# Revit family: Plumbing-Flushometer-Sloan-Valve-Royal-611-ESS-WB_
name_source: partatom
category: Plumbing Fixtures
units: mm (PartAtom-declared; Revit-internal decimal feet)

## family parameters
Cut with Voids When Loaded = Yes
Host = Face
Maintain Annotation Orientation = No
OmniClass Number = 23.45.05.14.99
Part Type = Normal
Room Calculation Point = No
Round Connector Dimension = Use Diameter
Shared = No

## types (3) — shared parameters
Apparent Load = 0 VA
Assembly Code = D2020300
CW Connection = Yes
Centerline of Supply from Top of Fixture = 14 1/2"
Centerline of Supply to Centerline of Valve = 5"
Connector Description = Electrical Connection
Current = 0 A
Default Elevation = 0"
Edition number = 1
HW Connection = No
Hardwired = Yes
Keynote = 15410
L Dimension = 3"
Manufacturer = Sloan Valve
Number of Poles = 1
Operating Water Pressure = 15 – 80 PSI (103 – 552 kPa)
Power Factor = 1
Product data url = https://bimobject.com
URL = www.sloanvalve.com
Valve Pressure Drop = 0.00 psi
Vent Connection = No
Version = 1
Voltage = 24 V
Waste Connection = No
Water Inlet Connection Description = Water Inlet Connection
Water Inlet Connection Diameter = 1"
zero-valued in all types: CWFU, HWFU, WFU

## per-type parameters (varying)
| type | Description | Flush Rate | Part Number | Product Material |
| ROYAL 611 ESS WB-1.28-HW | 1.28 gpf, Rough Brass Finish, Fixture Connection Rear Spud, Single Flush, Electrical Override, Hardwired, Sensor-Operated, Front Accessible Wall Box, Royal® Concealed Sensor Hardwired Water Closet Flushometer. | 1.28 gpf (4.8 Lpf) | 34581001 | Sloan Valve - Finish - Polished Chrome |
| ROYAL 611 ESS WB-1.6-HW | 1.6 gpf, Polished Chrome Finish, Fixture Connection Rear Spud, Single Flush, Electrical Override, Hardwired, Solenoid-Operated, 24V, Front Accessible Wall Box, Royal® Concealed Sensor Hardwired Water Closet Flushometer. | 1.6 gpf (6.0 Lpf) | 3918330 | Sloan Valve - Finish - Polished Chrome |
| ROYAL 611 ESS WB-3.5-HW | 3.5 gpf, Polished Chrome Finish, Fixture Connection Rear Spud, Single Flush, Electrical Override, Hardwired, Sensor-Operated, Front Accessible Wall Box, Royal® Concealed Sensor Hardwired Water Closet Flushometer. | 3.5 gpf (13.2 Lpf) | 3918938 | Sloan Valve - Finish - Rough Brass |

note: column(s) folded — value = type name in every type: Model

## geometry (parser evidence)
native form markers: Sweep x7
no freeform markers — native parametric forms only
